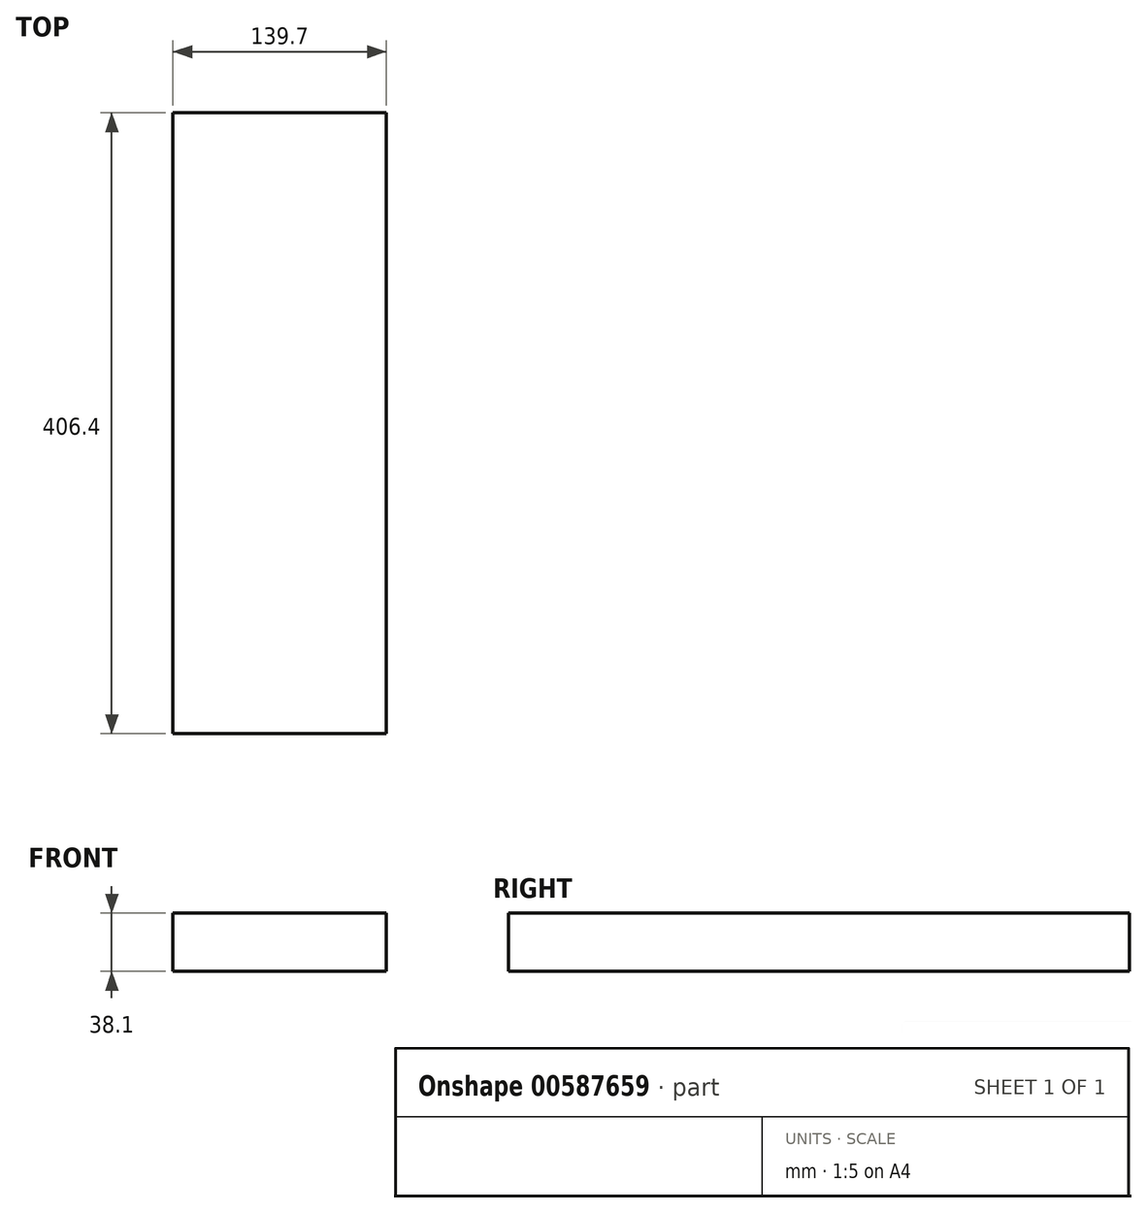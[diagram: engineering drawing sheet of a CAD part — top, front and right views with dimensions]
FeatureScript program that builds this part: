
annotation { "Feature Type Name" : "Feature", "Feature Type Description" : "" }
export const myFeature = defineFeature(function(context is Context, id is Id, definition is map)
    precondition{}
    {
        {
            var Q0;
            Q0=qCreatedBy(makeId("Front.planeOp"),FACE);
            var sketch = newSketch(context, id + "F0", { "sketchPlane" : qUnion([Q0])});
            skLineSegment(sketch, "E0.bottom", {"start": v(-69.85, 19.05) * mm, "end": v(69.85, 19.05) * mm});
            skLineSegment(sketch, "E0.top", {"start": v(-69.85, -19.05) * mm, "end": v(69.85, -19.05) * mm});
            skLineSegment(sketch, "E0.left", {"start": v(-69.85, 19.05) * mm, "end": v(-69.85, -19.05) * mm});
            skLineSegment(sketch, "E0.right", {"start": v(69.85, 19.05) * mm, "end": v(69.85, -19.05) * mm});
            skLineSegment(sketch, "E1", {"start": v(0, 0) * mm, "end": v(0, 19.05) * mm, "construction": true});
            skLineSegment(sketch, "E2", {"start": v(0, 0) * mm, "end": v(-69.85, 0) * mm, "construction": true});
            skSolve(sketch);
        }
        {
            var Q0;
            Q0 = qSketchRegion(id + "F0", true);
            extrude(context, id + "F1", {"entities" : qUnion([Q0]), "oppositeDirection" : true, "depth" : 406.4 * mm, "offsetDistance" : 25.4 * mm});
        }
    });
